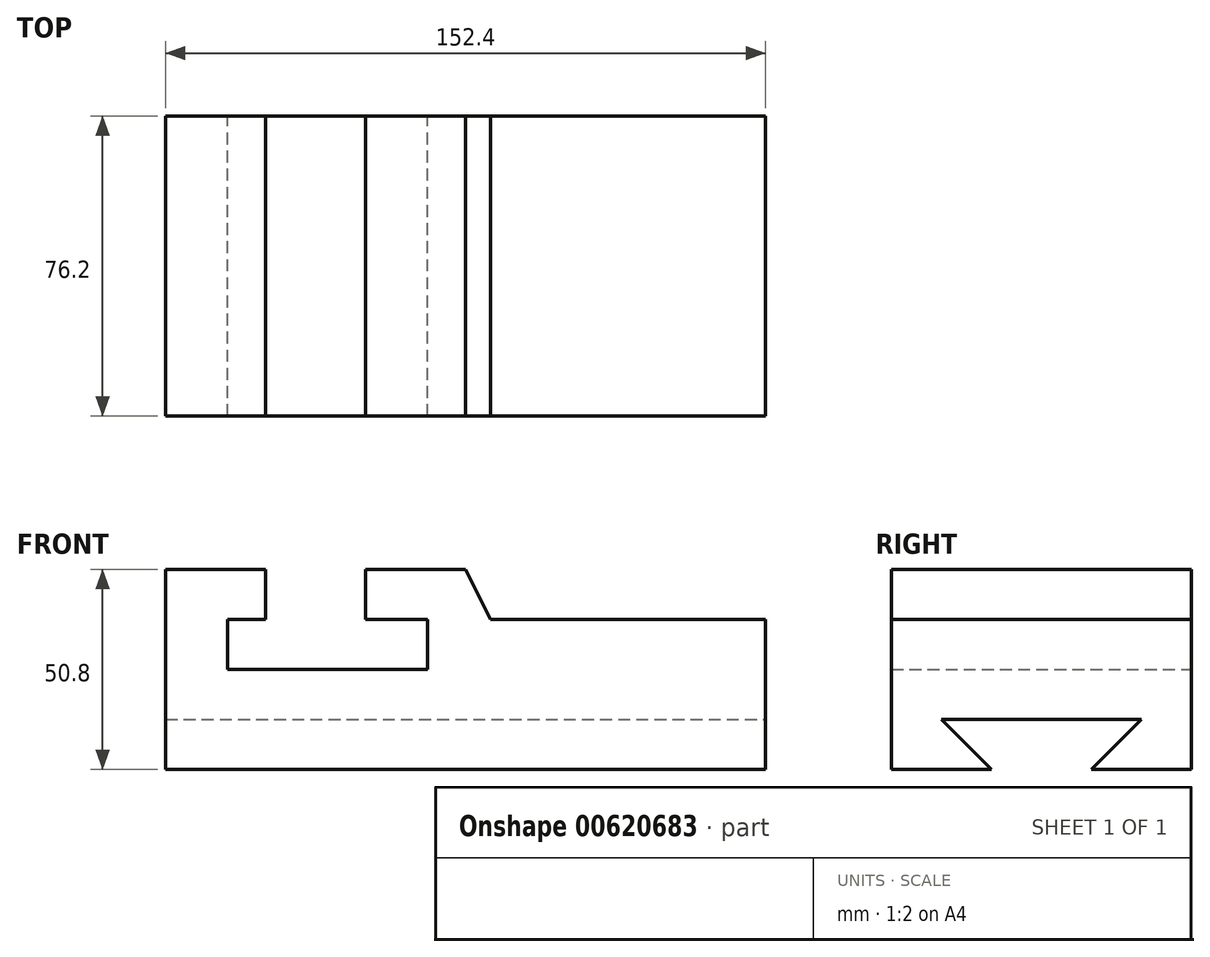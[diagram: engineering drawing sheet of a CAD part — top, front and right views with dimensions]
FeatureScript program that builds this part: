
annotation { "Feature Type Name" : "Feature", "Feature Type Description" : "" }
export const myFeature = defineFeature(function(context is Context, id is Id, definition is map)
    precondition{}
    {
        {
            var Q0;
            Q0=qCreatedBy(makeId("Front.planeOp"),FACE);
            var sketch = newSketch(context, id + "F0", { "sketchPlane" : qUnion([Q0])});
            skLineSegment(sketch, "E0", {"start": v(0, 0) * mm, "end": v(0, 50.8) * mm});
            skLineSegment(sketch, "E1", {"start": v(0, 50.8) * mm, "end": v(25.4, 50.8) * mm});
            skLineSegment(sketch, "E2", {"start": v(25.4, 50.8) * mm, "end": v(25.4, 38.1) * mm});
            skLineSegment(sketch, "E3", {"start": v(25.4, 38.1) * mm, "end": v(15.7, 38.1) * mm});
            skLineSegment(sketch, "E4", {"start": v(15.7, 38.1) * mm, "end": v(15.7, 25.4) * mm});
            skLineSegment(sketch, "E5", {"start": v(15.7, 25.4) * mm, "end": v(66.5, 25.4) * mm});
            skLineSegment(sketch, "E6", {"start": v(66.5, 25.4) * mm, "end": v(66.5, 38.1) * mm});
            skLineSegment(sketch, "E7", {"start": v(66.5, 38.1) * mm, "end": v(50.8, 38.1) * mm});
            skLineSegment(sketch, "E8", {"start": v(50.8, 38.1) * mm, "end": v(50.8, 50.8) * mm});
            skLineSegment(sketch, "E9", {"start": v(50.8, 50.8) * mm, "end": v(76.2, 50.8) * mm});
            skLineSegment(sketch, "E10", {"start": v(76.2, 50.8) * mm, "end": v(82.55, 38.1) * mm});
            skLineSegment(sketch, "E11", {"start": v(82.55, 38.1) * mm, "end": v(152.4, 38.1) * mm});
            skLineSegment(sketch, "E12", {"start": v(152.4, 38.1) * mm, "end": v(152.4, 0) * mm});
            skLineSegment(sketch, "E13", {"start": v(152.4, 0) * mm, "end": v(0, 0) * mm});
            skSolve(sketch);
        }
        {
            var Q0;
            Q0=makeQuery(id+"F0.imprint","IMPRINT",FACE,{"disambiguationData":[TD([[makeQuery(id+"F0.imprint","IMPRINT",EDGE,{"derivedFrom":sQuery(id+"F0.wireOp",EDGE,"E0")}),-1.0]])]});
            extrude(context, id + "F1", {"entities" : qUnion([Q0]), "depth" : 76.2 * mm, "offsetDistance" : 25.4 * mm});
        }
        {
            var Q0;
            Q0=makeQuery(id+"F1.opExtrude","SWEPT_FACE",FACE,{"disambiguationData":[OSD([sQuery(id+"F0.wireOp",EDGE,"E12")])]});
            var sketch = newSketch(context, id + "F2", { "sketchPlane" : qUnion([Q0])});
            skLineSegment(sketch, "E14", {"start": v(-50.8, 0) * mm, "end": v(-63.5, 12.7) * mm});
            skLineSegment(sketch, "E15", {"start": v(-63.5, 12.7) * mm, "end": v(-12.7, 12.7) * mm});
            skLineSegment(sketch, "E16", {"start": v(-12.7, 12.7) * mm, "end": v(-25.4, 0) * mm});
            skSolve(sketch);
        }
        {
            var Q0;
            {var subQ0=sQuery(id+"F2.wireOp",EDGE,"E14");Q0=makeQuery(id+"F2.imprint","IMPRINT",FACE,{"disambiguationData":[TD([[makeQuery(id+"F2.imprint","IMPRINT",EDGE,{"derivedFrom":subQ0}),-1.0]])]});}
            extrude(context, id + "F3", {"entities" : qUnion([Q0]), "operationType" : NewBodyOperationType.REMOVE, "oppositeDirection" : true, "depth" : 209.3 * mm, "offsetDistance" : 25.4 * mm});
        }
    });
